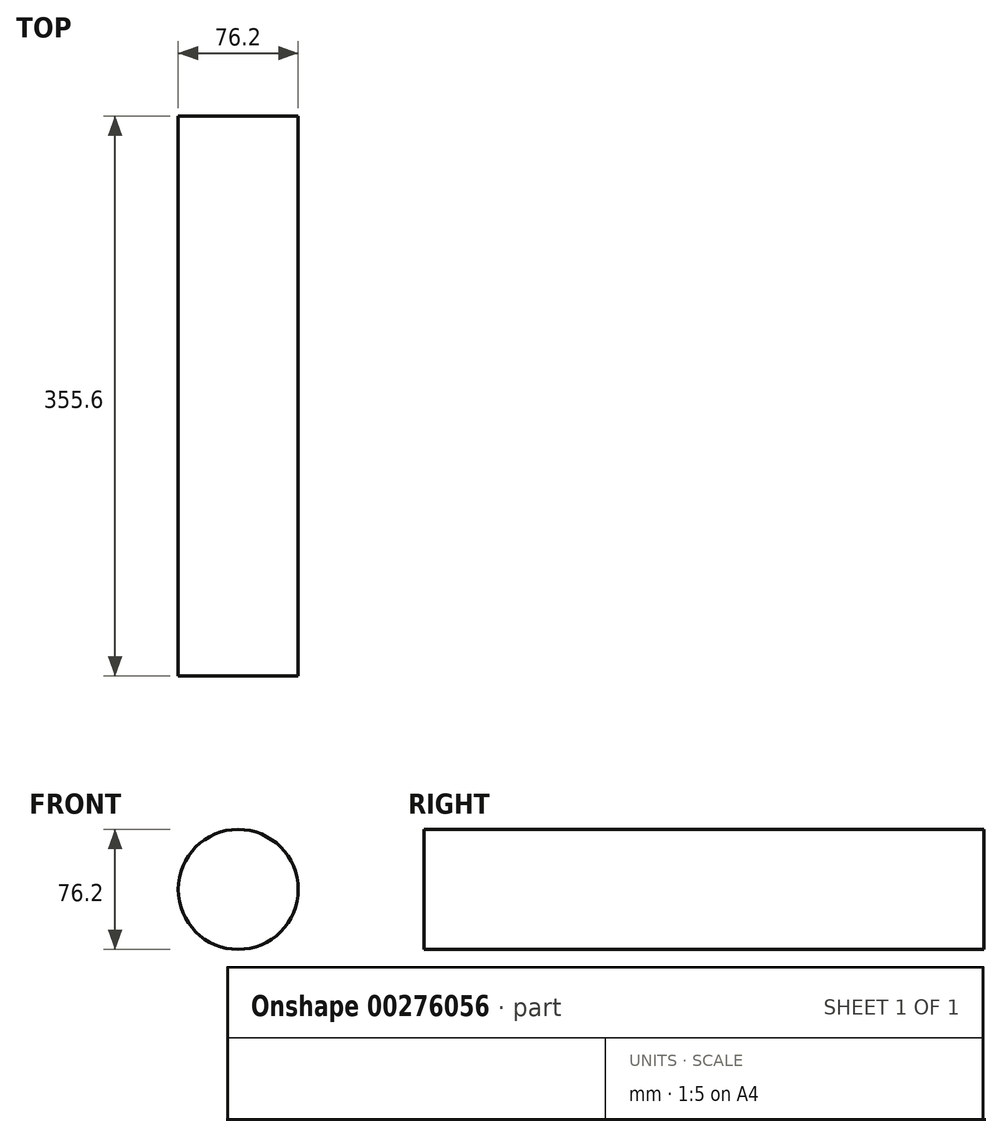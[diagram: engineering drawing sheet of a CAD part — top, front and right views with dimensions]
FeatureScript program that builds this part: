
annotation { "Feature Type Name" : "Feature", "Feature Type Description" : "" }
export const myFeature = defineFeature(function(context is Context, id is Id, definition is map)
    precondition{}
    {
        {
            var Q0;
            Q0=qCreatedBy(makeId("Front.planeOp"),FACE);
            var sketch = newSketch(context, id + "F0", { "sketchPlane" : qUnion([Q0])});
            skCircle(sketch, "E0", {"center": v(0, 0) * mm, "radius": 38.1 * mm});
            skSolve(sketch);
        }
        {
            var Q0;
            Q0=qSketchRegion(id+"F0",true);
            extrude(context, id + "F1", {"entities" : qUnion([Q0]), "depth" : 355.6 * mm});
        }
    });
